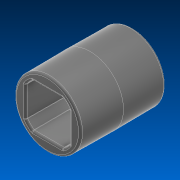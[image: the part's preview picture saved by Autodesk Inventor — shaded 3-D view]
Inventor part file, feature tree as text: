
AUTODESK INVENTOR PART (.ipt)
format: ipt  version: 2022.2 (Build 262287000, 287)  size: 217,088 bytes
history: native  units: in
note: dims shown in document units (in); Inventor stores cm internally (conversion verified against a paired STEP export)
features: fillet x1
ambient origin geometry x8: Origin, YZ Plane, XZ Plane, XY Plane, X Axis, Y Axis, Z Axis, Center Point
bodies: Solid1 (feature_tree)
feature tree (1):
  fillet  "Fillet1"  [1 undecoded]
note: 1 required parameter value undecoded (feature->parameter linkage not recoverable at this tier; creation-order binding heuristic only, values carry confidence <= 0.55)
